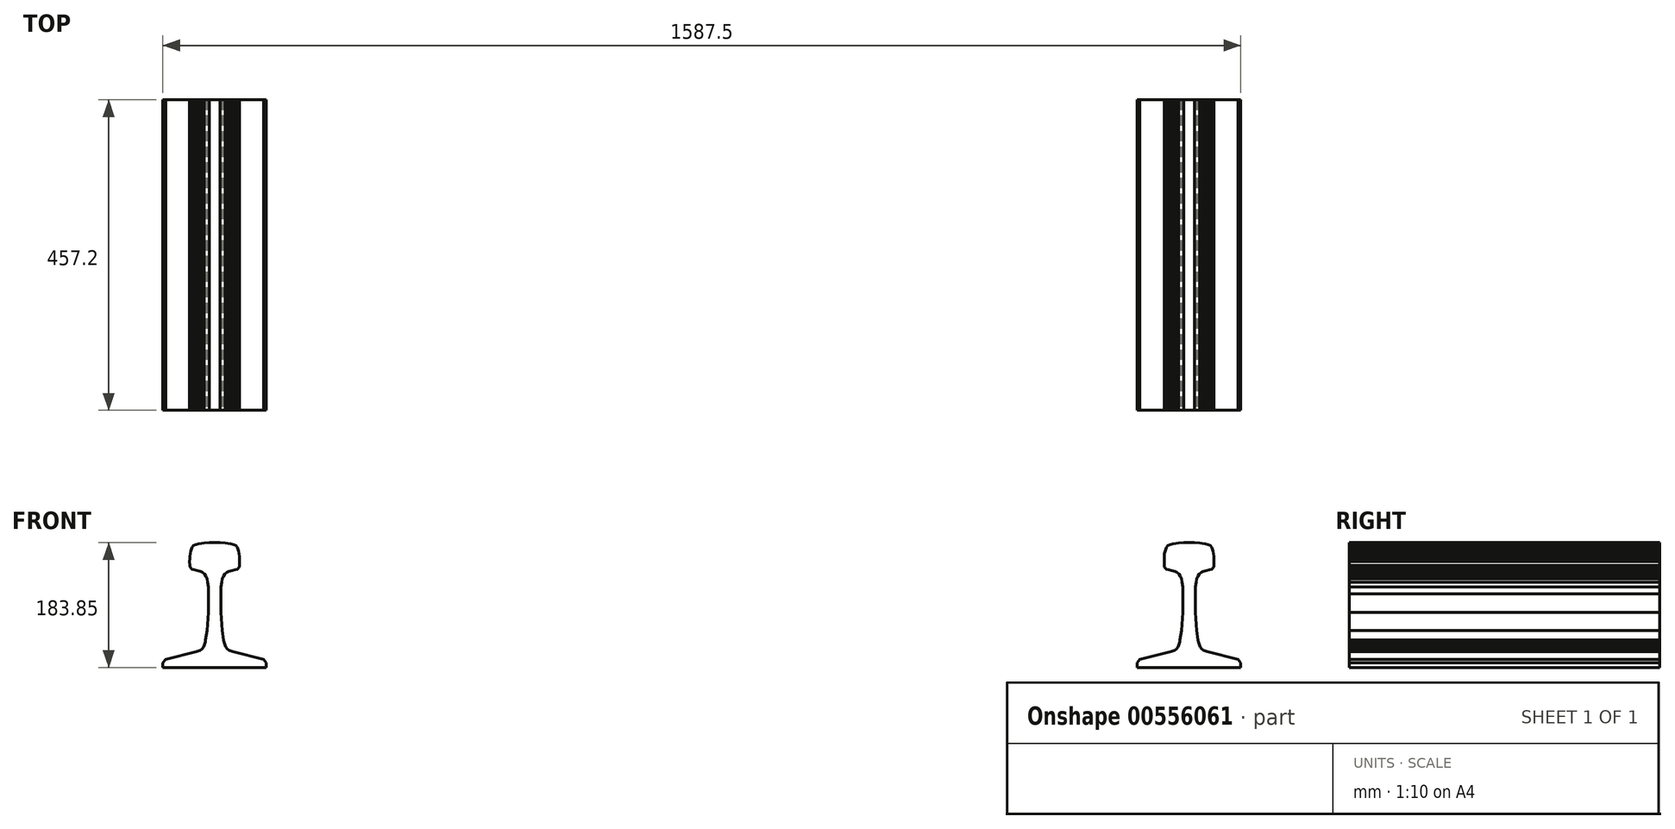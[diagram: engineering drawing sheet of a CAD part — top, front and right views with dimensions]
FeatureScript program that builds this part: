
annotation { "Feature Type Name" : "Feature", "Feature Type Description" : "" }
export const myFeature = defineFeature(function(context is Context, id is Id, definition is map)
    precondition{}
    {
        {
            var Q0;
            Q0=qCreatedBy(makeId("Front.planeOp"),FACE);
            var sketch = newSketch(context, id + "F0", { "sketchPlane" : qUnion([Q0])});
            skLineSegment(sketch, "E0", {"start": v(-76.2, -57.1) * mm, "end": v(76.2, -57.1) * mm});
            skLineSegment(sketch, "E1", {"start": v(-76.2, -57.1) * mm, "end": v(-76.2, -46.22) * mm});
            skLineSegment(sketch, "E2", {"start": v(-26.84, -33.73) * mm, "end": v(-76.2, -46.22) * mm});
            skPoint(sketch, "E3.startSnap0", {"position": v(0, -57.1) * mm});
            skPoint(sketch, "E3.endSnap0", {"position": v(0, -57.1) * mm});
            skLineSegment(sketch, "E4.MirrorCS", {"start": v(26.84, -33.73) * mm, "end": v(76.2, -46.22) * mm});
            skLineSegment(sketch, "E5.MirrorCS", {"start": v(0, -26.94) * mm, "end": v(0, -26.94) * mm});
            skLineSegment(sketch, "E6.MirrorCS", {"start": v(76.2, -57.1) * mm, "end": v(76.2, -46.22) * mm});
            skLineSegment(sketch, "E7", {"start": v(-26.84, -33.73) * mm, "end": v(-21.16, -31.84) * mm});
            skLineSegment(sketch, "E8", {"start": v(-21.16, -31.84) * mm, "end": v(-18.7, -29.61) * mm});
            skLineSegment(sketch, "E9", {"start": v(-18.7, -29.61) * mm, "end": v(-16.22, -26.55) * mm});
            skLineSegment(sketch, "E10", {"start": v(-16.22, -26.55) * mm, "end": v(-14.69, -22.9) * mm});
            skLineSegment(sketch, "E11", {"start": v(-14.69, -22.9) * mm, "end": v(-13.49, -19.14) * mm});
            skLineSegment(sketch, "E12", {"start": v(-13.49, -19.14) * mm, "end": v(-13.3, -16.85) * mm});
            skLineSegment(sketch, "E13", {"start": v(-13.3, -16.85) * mm, "end": v(-10.94, -2.66) * mm});
            skLineSegment(sketch, "E14", {"start": v(-10.94, -2.66) * mm, "end": v(-9.17, 23.94) * mm});
            skLineSegment(sketch, "E15", {"start": v(-9.17, 23.94) * mm, "end": v(-9.1, 51.27) * mm});
            skLineSegment(sketch, "E16", {"start": v(-9.1, 51.27) * mm, "end": v(-9.47, 61.37) * mm});
            skLineSegment(sketch, "E17", {"start": v(-36.63, 93.52) * mm, "end": v(-36.6, 93.52) * mm});
            skLineSegment(sketch, "E18", {"start": v(-9.47, 61.37) * mm, "end": v(-10.2, 68.53) * mm});
            skLineSegment(sketch, "E19", {"start": v(-10.2, 68.53) * mm, "end": v(-11.42, 73.4) * mm});
            skLineSegment(sketch, "E20", {"start": v(-11.42, 73.4) * mm, "end": v(-12.99, 77.66) * mm});
            skLineSegment(sketch, "E21", {"start": v(-12.99, 77.66) * mm, "end": v(-14.98, 80.45) * mm});
            skLineSegment(sketch, "E22", {"start": v(-14.98, 80.45) * mm, "end": v(-18.1, 83) * mm});
            skLineSegment(sketch, "E23", {"start": v(-18.1, 83) * mm, "end": v(-20.68, 84.15) * mm});
            skLineSegment(sketch, "E24", {"start": v(-20.68, 84.15) * mm, "end": v(-25.92, 85.98) * mm});
            skLineSegment(sketch, "E25", {"start": v(-25.92, 85.98) * mm, "end": v(-30.18, 87.13) * mm});
            skLineSegment(sketch, "E26", {"start": v(-30.18, 87.13) * mm, "end": v(-33.1, 87.75) * mm});
            skLineSegment(sketch, "E27", {"start": v(-33.1, 87.75) * mm, "end": v(-34.18, 88.3) * mm});
            skLineSegment(sketch, "E28", {"start": v(-34.18, 88.3) * mm, "end": v(-35.39, 89.62) * mm});
            skLineSegment(sketch, "E29", {"start": v(-35.39, 89.62) * mm, "end": v(-36.17, 91) * mm});
            skLineSegment(sketch, "E30", {"start": v(-36.17, 91) * mm, "end": v(-36.4, 91.97) * mm});
            skLineSegment(sketch, "E31", {"start": v(-36.4, 91.97) * mm, "end": v(-36.6, 93.51) * mm});
            skLineSegment(sketch, "E32", {"start": v(-36.6, 93.51) * mm, "end": v(-36.83, 98.88) * mm});
            skLineSegment(sketch, "E33", {"start": v(-36.83, 98.88) * mm, "end": v(-36.67, 103.67) * mm});
            skLineSegment(sketch, "E34", {"start": v(-36.67, 103.67) * mm, "end": v(-36.4, 106.65) * mm});
            skLineSegment(sketch, "E35", {"start": v(-36.4, 106.65) * mm, "end": v(-36.18, 110.32) * mm});
            skLineSegment(sketch, "E36", {"start": v(-36.18, 110.32) * mm, "end": v(-35.56, 114.28) * mm});
            skLineSegment(sketch, "E37", {"start": v(-35.56, 114.28) * mm, "end": v(-34.24, 117.98) * mm});
            skLineSegment(sketch, "E38", {"start": v(-34.24, 117.98) * mm, "end": v(-33.33, 119.88) * mm});
            skLineSegment(sketch, "E39", {"start": v(-33.33, 119.88) * mm, "end": v(-31.13, 122.46) * mm});
            skLineSegment(sketch, "E40", {"start": v(-31.13, 122.46) * mm, "end": v(-28.22, 124.04) * mm});
            skLineSegment(sketch, "E41", {"start": v(-28.22, 124.04) * mm, "end": v(-24.03, 125.35) * mm});
            skLineSegment(sketch, "E42", {"start": v(-24.03, 125.35) * mm, "end": v(-19.54, 126) * mm});
            skLineSegment(sketch, "E43.MirrorCS", {"start": v(36.4, 91.97) * mm, "end": v(36.6, 93.51) * mm});
            skLineSegment(sketch, "E44.MirrorCS", {"start": v(36.17, 91) * mm, "end": v(36.4, 91.97) * mm});
            skLineSegment(sketch, "E45.MirrorCS", {"start": v(13.49, -19.14) * mm, "end": v(13.3, -16.85) * mm});
            skLineSegment(sketch, "E46.MirrorCS", {"start": v(36.67, 103.67) * mm, "end": v(36.4, 106.65) * mm});
            skLineSegment(sketch, "E47.MirrorCS", {"start": v(20.68, 84.15) * mm, "end": v(25.92, 85.98) * mm});
            skLineSegment(sketch, "E48.MirrorCS", {"start": v(31.13, 122.46) * mm, "end": v(28.22, 124.04) * mm});
            skLineSegment(sketch, "E49.MirrorCS", {"start": v(36.6, 93.51) * mm, "end": v(36.83, 98.88) * mm});
            skLineSegment(sketch, "E50.MirrorCS", {"start": v(16.22, -26.55) * mm, "end": v(14.69, -22.9) * mm});
            skLineSegment(sketch, "E51.MirrorCS", {"start": v(34.18, 88.3) * mm, "end": v(35.39, 89.62) * mm});
            skLineSegment(sketch, "E52.MirrorCS", {"start": v(14.69, -22.9) * mm, "end": v(13.49, -19.14) * mm});
            skLineSegment(sketch, "E53.MirrorCS", {"start": v(12.99, 77.66) * mm, "end": v(14.98, 80.45) * mm});
            skLineSegment(sketch, "E54.MirrorCS", {"start": v(35.56, 114.28) * mm, "end": v(34.24, 117.98) * mm});
            skLineSegment(sketch, "E55.MirrorCS", {"start": v(28.22, 124.04) * mm, "end": v(24.03, 125.35) * mm});
            skLineSegment(sketch, "E56.MirrorCS", {"start": v(25.92, 85.98) * mm, "end": v(30.18, 87.13) * mm});
            skLineSegment(sketch, "E57.MirrorCS", {"start": v(26.84, -33.73) * mm, "end": v(21.16, -31.84) * mm});
            skLineSegment(sketch, "E58.MirrorCS", {"start": v(18.1, 83) * mm, "end": v(20.68, 84.15) * mm});
            skLineSegment(sketch, "E59.MirrorCS", {"start": v(21.16, -31.84) * mm, "end": v(18.7, -29.61) * mm});
            skLineSegment(sketch, "E60.MirrorCS", {"start": v(14.98, 80.45) * mm, "end": v(18.1, 83) * mm});
            skLineSegment(sketch, "E61.MirrorCS", {"start": v(33.1, 87.75) * mm, "end": v(34.18, 88.3) * mm});
            skLineSegment(sketch, "E62.MirrorCS", {"start": v(33.33, 119.88) * mm, "end": v(31.13, 122.46) * mm});
            skLineSegment(sketch, "E63.MirrorCS", {"start": v(30.18, 87.13) * mm, "end": v(33.1, 87.75) * mm});
            skLineSegment(sketch, "E64.MirrorCS", {"start": v(10.2, 68.53) * mm, "end": v(11.42, 73.4) * mm});
            skLineSegment(sketch, "E65.MirrorCS", {"start": v(34.24, 117.98) * mm, "end": v(33.33, 119.88) * mm});
            skLineSegment(sketch, "E66.MirrorCS", {"start": v(11.42, 73.4) * mm, "end": v(12.99, 77.66) * mm});
            skLineSegment(sketch, "E67.MirrorCS", {"start": v(24.03, 125.35) * mm, "end": v(19.54, 126) * mm});
            skLineSegment(sketch, "E68.MirrorCS", {"start": v(18.7, -29.61) * mm, "end": v(16.22, -26.55) * mm});
            skLineSegment(sketch, "E69.MirrorCS", {"start": v(35.39, 89.62) * mm, "end": v(36.17, 91) * mm});
            skLineSegment(sketch, "E70.MirrorCS", {"start": v(36.18, 110.32) * mm, "end": v(35.56, 114.28) * mm});
            skLineSegment(sketch, "E71.MirrorCS", {"start": v(36.4, 106.65) * mm, "end": v(36.18, 110.32) * mm});
            skLineSegment(sketch, "E72.MirrorCS", {"start": v(9.47, 61.37) * mm, "end": v(10.2, 68.53) * mm});
            skLineSegment(sketch, "E73.MirrorCS", {"start": v(15.45, 126.6) * mm, "end": v(15.43, 126.61) * mm});
            skLineSegment(sketch, "E74.MirrorCS", {"start": v(36.83, 98.88) * mm, "end": v(36.67, 103.67) * mm});
            skLineSegment(sketch, "E75.MirrorCS", {"start": v(10.94, -2.66) * mm, "end": v(9.17, 23.94) * mm});
            skLineSegment(sketch, "E76.MirrorCS", {"start": v(9.1, 51.27) * mm, "end": v(9.47, 61.37) * mm});
            skLineSegment(sketch, "E77.MirrorCS", {"start": v(13.3, -16.85) * mm, "end": v(10.94, -2.66) * mm});
            skLineSegment(sketch, "E78.MirrorCS", {"start": v(9.17, 23.94) * mm, "end": v(9.1, 51.27) * mm});
            skPoint(sketch, "E79.start.orphan", {"position": v(-15.43, 126.61) * mm});
            skLineSegment(sketch, "E80", {"start": v(-19.54, 126) * mm, "end": v(-15.43, 126.4) * mm});
            skLineSegment(sketch, "E81", {"start": v(-15.43, 126.4) * mm, "end": v(-8, 126.76) * mm});
            skLineSegment(sketch, "E82", {"start": v(-8, 126.76) * mm, "end": v(0, 126.76) * mm});
            skLineSegment(sketch, "E83.MirrorCS", {"start": v(8, 126.76) * mm, "end": v(0, 126.76) * mm});
            skLineSegment(sketch, "E84.MirrorCS", {"start": v(15.43, 126.4) * mm, "end": v(8, 126.76) * mm});
            skLineSegment(sketch, "E85.MirrorCS", {"start": v(19.54, 126) * mm, "end": v(15.43, 126.4) * mm});
            skPoint(sketch, "E86.orphan", {"position": v(-76.2, -26.94) * mm});
            skPoint(sketch, "E87.orphan", {"position": v(-31.72, -14.5) * mm});
            skPoint(sketch, "E88.end.orphan", {"position": v(-76.21, 41.14) * mm});
            skPoint(sketch, "E88.start.orphan", {"position": v(-76.21, -8.79) * mm});
            skLineSegment(sketch, "E89", {"start": v(76.2, -57.1) * mm, "end": v(76.2, -57.1) * mm});
            skPoint(sketch, "E90.orphan", {"position": v(76.2, -26.94) * mm});
            skPoint(sketch, "E91.MirrorCS.end.orphan", {"position": v(76.21, -8.79) * mm});
            skPoint(sketch, "E91.MirrorCS.start.orphan", {"position": v(31.72, -14.5) * mm});
            skPoint(sketch, "E92.orphan", {"position": v(0, -26.94) * mm});
            skLineSegment(sketch, "E93.trimOffspring", {"start": v(36.6, 93.52) * mm, "end": v(37.03, 93.52) * mm});
            skPoint(sketch, "E94.trimOffspring.end.orphan", {"position": v(0, 152.1) * mm});
            skPoint(sketch, "E3.start.orphan", {"position": v(0, -57.1) * mm});
            skLineSegment(sketch, "E95.MirrorCS", {"start": v(1470.49, 89.62) * mm, "end": v(1471.27, 91) * mm});
            skLineSegment(sketch, "E96.MirrorCS", {"start": v(1471.73, 93.52) * mm, "end": v(1471.7, 93.52) * mm});
            skLineSegment(sketch, "E97.MirrorCS", {"start": v(1468.2, 87.75) * mm, "end": v(1469.28, 88.3) * mm});
            skLineSegment(sketch, "E98.MirrorCS", {"start": v(1471.27, 91) * mm, "end": v(1471.5, 91.97) * mm});
            skLineSegment(sketch, "E99.MirrorCS", {"start": v(1469.28, 88.3) * mm, "end": v(1470.49, 89.62) * mm});
            skLineSegment(sketch, "E100.MirrorCS", {"start": v(1471.5, 91.97) * mm, "end": v(1471.7, 93.51) * mm});
            skLineSegment(sketch, "E101.MirrorCS", {"start": v(1471.93, 98.88) * mm, "end": v(1471.77, 103.67) * mm});
            skLineSegment(sketch, "E102.MirrorCS", {"start": v(1461.02, 85.98) * mm, "end": v(1465.28, 87.13) * mm});
            skLineSegment(sketch, "E103.MirrorCS", {"start": v(1465.28, 87.13) * mm, "end": v(1468.2, 87.75) * mm});
            skLineSegment(sketch, "E104.MirrorCS", {"start": v(1471.7, 93.51) * mm, "end": v(1471.93, 98.88) * mm});
            skLineSegment(sketch, "E105.MirrorCS", {"start": v(1471.77, 103.67) * mm, "end": v(1471.5, 106.65) * mm});
            skLineSegment(sketch, "E106.MirrorCS", {"start": v(1470.66, 114.28) * mm, "end": v(1469.34, 117.98) * mm});
            skLineSegment(sketch, "E107.MirrorCS", {"start": v(1398.93, 91) * mm, "end": v(1398.7, 91.97) * mm});
            skLineSegment(sketch, "E108.MirrorCS", {"start": v(1398.7, 91.97) * mm, "end": v(1398.5, 93.51) * mm});
            skLineSegment(sketch, "E109.MirrorCS", {"start": v(1469.34, 117.98) * mm, "end": v(1468.43, 119.88) * mm});
            skLineSegment(sketch, "E110.MirrorCS", {"start": v(1471.5, 106.65) * mm, "end": v(1471.28, 110.32) * mm});
            skLineSegment(sketch, "E111.MirrorCS", {"start": v(1400.92, 88.3) * mm, "end": v(1399.71, 89.62) * mm});
            skLineSegment(sketch, "E112.MirrorCS", {"start": v(1471.28, 110.32) * mm, "end": v(1470.66, 114.28) * mm});
            skLineSegment(sketch, "E113.MirrorCS", {"start": v(1404.92, 87.13) * mm, "end": v(1402, 87.75) * mm});
            skLineSegment(sketch, "E114.MirrorCS", {"start": v(1466.23, 122.46) * mm, "end": v(1463.32, 124.04) * mm});
            skLineSegment(sketch, "E115.MirrorCS", {"start": v(1402, 87.75) * mm, "end": v(1400.92, 88.3) * mm});
            skLineSegment(sketch, "E116.MirrorCS", {"start": v(1398.5, 93.51) * mm, "end": v(1398.27, 98.88) * mm});
            skLineSegment(sketch, "E117.MirrorCS", {"start": v(1409.18, 85.98) * mm, "end": v(1404.92, 87.13) * mm});
            skLineSegment(sketch, "E118.MirrorCS", {"start": v(1358.9, -57.1) * mm, "end": v(1358.9, -46.22) * mm});
            skLineSegment(sketch, "E119.MirrorCS", {"start": v(1398.5, 93.52) * mm, "end": v(1398.07, 93.52) * mm});
            skLineSegment(sketch, "E120.MirrorCS", {"start": v(1398.27, 98.88) * mm, "end": v(1398.43, 103.67) * mm});
            skLineSegment(sketch, "E121.MirrorCS", {"start": v(1399.71, 89.62) * mm, "end": v(1398.93, 91) * mm});
            skLineSegment(sketch, "E122.MirrorCS", {"start": v(1468.43, 119.88) * mm, "end": v(1466.23, 122.46) * mm});
            skLineSegment(sketch, "E123.MirrorCS", {"start": v(1450.08, 80.45) * mm, "end": v(1453.2, 83) * mm});
            skLineSegment(sketch, "E124.MirrorCS", {"start": v(1419.65, 126.6) * mm, "end": v(1419.67, 126.61) * mm});
            skLineSegment(sketch, "E125.MirrorCS", {"start": v(1451.32, -26.55) * mm, "end": v(1449.79, -22.9) * mm});
            skLineSegment(sketch, "E126.MirrorCS", {"start": v(1420.41, -22.9) * mm, "end": v(1421.61, -19.14) * mm});
            skLineSegment(sketch, "E127.MirrorCS", {"start": v(1400.86, 117.98) * mm, "end": v(1401.77, 119.88) * mm});
            skLineSegment(sketch, "E128.MirrorCS", {"start": v(1418.88, -26.55) * mm, "end": v(1420.41, -22.9) * mm});
            skLineSegment(sketch, "E129.MirrorCS", {"start": v(1456.26, -31.84) * mm, "end": v(1453.8, -29.61) * mm});
            skLineSegment(sketch, "E130.MirrorCS", {"start": v(1449.79, -22.9) * mm, "end": v(1448.59, -19.14) * mm});
            skLineSegment(sketch, "E131.MirrorCS", {"start": v(1448.59, -19.14) * mm, "end": v(1448.4, -16.85) * mm});
            skLineSegment(sketch, "E132.MirrorCS", {"start": v(1421.61, -19.14) * mm, "end": v(1421.8, -16.85) * mm});
            skLineSegment(sketch, "E133.MirrorCS", {"start": v(1403.97, 122.46) * mm, "end": v(1406.88, 124.04) * mm});
            skLineSegment(sketch, "E134.MirrorCS", {"start": v(1448.09, 77.66) * mm, "end": v(1450.08, 80.45) * mm});
            skLineSegment(sketch, "E135.MirrorCS", {"start": v(1463.32, 124.04) * mm, "end": v(1459.13, 125.35) * mm});
            skLineSegment(sketch, "E136.MirrorCS", {"start": v(1423.68, 73.4) * mm, "end": v(1422.11, 77.66) * mm});
            skLineSegment(sketch, "E137.MirrorCS", {"start": v(1398.7, 106.65) * mm, "end": v(1398.92, 110.32) * mm});
            skLineSegment(sketch, "E138.MirrorCS", {"start": v(1399.54, 114.28) * mm, "end": v(1400.86, 117.98) * mm});
            skLineSegment(sketch, "E139.MirrorCS", {"start": v(1419.67, 126.4) * mm, "end": v(1427.1, 126.76) * mm});
            skLineSegment(sketch, "E140.MirrorCS", {"start": v(1461.94, -33.73) * mm, "end": v(1456.26, -31.84) * mm});
            skLineSegment(sketch, "E141.MirrorCS", {"start": v(1406.88, 124.04) * mm, "end": v(1411.07, 125.35) * mm});
            skLineSegment(sketch, "E142.MirrorCS", {"start": v(1413.94, -31.84) * mm, "end": v(1416.4, -29.61) * mm});
            skLineSegment(sketch, "E143.MirrorCS", {"start": v(1398.43, 103.67) * mm, "end": v(1398.7, 106.65) * mm});
            skLineSegment(sketch, "E144.MirrorCS", {"start": v(1411.07, 125.35) * mm, "end": v(1415.56, 126) * mm});
            skLineSegment(sketch, "E145.MirrorCS", {"start": v(1453.2, 83) * mm, "end": v(1455.78, 84.15) * mm});
            skLineSegment(sketch, "E146.MirrorCS", {"start": v(1446.52, 73.4) * mm, "end": v(1448.09, 77.66) * mm});
            skLineSegment(sketch, "E147.MirrorCS", {"start": v(1455.78, 84.15) * mm, "end": v(1461.02, 85.98) * mm});
            skLineSegment(sketch, "E148.MirrorCS", {"start": v(1417, 83) * mm, "end": v(1414.42, 84.15) * mm});
            skLineSegment(sketch, "E149.MirrorCS", {"start": v(1398.92, 110.32) * mm, "end": v(1399.54, 114.28) * mm});
            skLineSegment(sketch, "E150.MirrorCS", {"start": v(1453.8, -29.61) * mm, "end": v(1451.32, -26.55) * mm});
            skLineSegment(sketch, "E151.MirrorCS", {"start": v(1415.56, 126) * mm, "end": v(1419.67, 126.4) * mm});
            skLineSegment(sketch, "E152.MirrorCS", {"start": v(1454.64, 126) * mm, "end": v(1450.53, 126.4) * mm});
            skLineSegment(sketch, "E153.MirrorCS", {"start": v(1416.4, -29.61) * mm, "end": v(1418.88, -26.55) * mm});
            skLineSegment(sketch, "E154.MirrorCS", {"start": v(1401.77, 119.88) * mm, "end": v(1403.97, 122.46) * mm});
            skLineSegment(sketch, "E155.MirrorCS", {"start": v(1448.4, -16.85) * mm, "end": v(1446.04, -2.66) * mm});
            skLineSegment(sketch, "E156.MirrorCS", {"start": v(1425.63, 61.37) * mm, "end": v(1424.9, 68.53) * mm});
            skLineSegment(sketch, "E157.MirrorCS", {"start": v(1427.1, 126.76) * mm, "end": v(1435.1, 126.76) * mm});
            skLineSegment(sketch, "E158.MirrorCS", {"start": v(1424.9, 68.53) * mm, "end": v(1423.68, 73.4) * mm});
            skLineSegment(sketch, "E159.MirrorCS", {"start": v(1443.1, 126.76) * mm, "end": v(1435.1, 126.76) * mm});
            skLineSegment(sketch, "E160.MirrorCS", {"start": v(1444.57, 61.37) * mm, "end": v(1445.3, 68.53) * mm});
            skLineSegment(sketch, "E161.MirrorCS", {"start": v(1450.53, 126.4) * mm, "end": v(1443.1, 126.76) * mm});
            skLineSegment(sketch, "E162.MirrorCS", {"start": v(1420.12, 80.45) * mm, "end": v(1417, 83) * mm});
            skLineSegment(sketch, "E163.MirrorCS", {"start": v(1408.26, -33.73) * mm, "end": v(1413.94, -31.84) * mm});
            skLineSegment(sketch, "E164.MirrorCS", {"start": v(1459.13, 125.35) * mm, "end": v(1454.64, 126) * mm});
            skLineSegment(sketch, "E165.MirrorCS", {"start": v(1445.3, 68.53) * mm, "end": v(1446.52, 73.4) * mm});
            skLineSegment(sketch, "E166.MirrorCS", {"start": v(1422.11, 77.66) * mm, "end": v(1420.12, 80.45) * mm});
            skLineSegment(sketch, "E167.MirrorCS", {"start": v(1444.2, 51.27) * mm, "end": v(1444.57, 61.37) * mm});
            skLineSegment(sketch, "E168.MirrorCS", {"start": v(1421.8, -16.85) * mm, "end": v(1424.16, -2.66) * mm});
            skLineSegment(sketch, "E169.MirrorCS", {"start": v(1414.42, 84.15) * mm, "end": v(1409.18, 85.98) * mm});
            skLineSegment(sketch, "E170.MirrorCS", {"start": v(1446.04, -2.66) * mm, "end": v(1444.27, 23.94) * mm});
            skPoint(sketch, "E171.MirrorP", {"position": v(1435.1, -57.1) * mm});
            skLineSegment(sketch, "E172.MirrorCS", {"start": v(1424.16, -2.66) * mm, "end": v(1425.93, 23.94) * mm});
            skLineSegment(sketch, "E173.MirrorCS", {"start": v(1426, 51.27) * mm, "end": v(1425.63, 61.37) * mm});
            skLineSegment(sketch, "E174.MirrorCS", {"start": v(1511.3, -57.1) * mm, "end": v(1511.3, -46.22) * mm});
            skLineSegment(sketch, "E175.MirrorCS", {"start": v(1358.9, -57.1) * mm, "end": v(1358.9, -57.1) * mm});
            skPoint(sketch, "E176.MirrorP", {"position": v(1435.1, -26.94) * mm});
            skPoint(sketch, "E177.MirrorP", {"position": v(1358.9, -26.94) * mm});
            skPoint(sketch, "E178.MirrorP", {"position": v(1511.3, -26.94) * mm});
            skPoint(sketch, "E179.MirrorP", {"position": v(1466.82, -14.5) * mm});
            skLineSegment(sketch, "E180.MirrorCS", {"start": v(1425.93, 23.94) * mm, "end": v(1426, 51.27) * mm});
            skPoint(sketch, "E181.MirrorP", {"position": v(1450.53, 126.61) * mm});
            skPoint(sketch, "E182.MirrorP", {"position": v(1358.89, -8.79) * mm});
            skLineSegment(sketch, "E183.MirrorCS", {"start": v(1444.27, 23.94) * mm, "end": v(1444.2, 51.27) * mm});
            skPoint(sketch, "E184.MirrorP", {"position": v(1403.38, -14.5) * mm});
            skLineSegment(sketch, "E185.MirrorCS", {"start": v(1461.94, -33.73) * mm, "end": v(1511.3, -46.22) * mm});
            skPoint(sketch, "E186.MirrorP", {"position": v(1511.31, -8.79) * mm});
            skLineSegment(sketch, "E187.MirrorCS", {"start": v(1435.1, -26.94) * mm, "end": v(1435.1, -26.94) * mm});
            skPoint(sketch, "E188.MirrorP", {"position": v(1511.31, 41.14) * mm});
            skLineSegment(sketch, "E189.MirrorCS", {"start": v(1511.3, -57.1) * mm, "end": v(1358.9, -57.1) * mm});
            skLineSegment(sketch, "E190.MirrorCS", {"start": v(1408.26, -33.73) * mm, "end": v(1358.9, -46.22) * mm});
            skPoint(sketch, "E191.MirrorP", {"position": v(1435.1, 152.1) * mm});
            skSolve(sketch);
        }
        {
            var Q0;
            Q0=qSketchRegion(id+"F0",true);
            extrude(context, id + "F1", {"entities" : qUnion([Q0]), "oppositeDirection" : true, "depth" : 457.2 * mm, "offsetDistance" : 25.4 * mm});
        }
        {
            var Q0;
            Q0=makeQuery(id+"F1.opExtrude","SWEPT_EDGE",EDGE,{"disambiguationData":[OSD([sQuery(id+"F0.wireOp",EDGE,"E4.MirrorCS"),sQuery(id+"F0.wireOp",EDGE,"E6.MirrorCS")])]});
            var Q1;
            Q1=makeQuery(id+"F1.opExtrude","SWEPT_EDGE",EDGE,{"disambiguationData":[OSD([sQuery(id+"F0.wireOp",EDGE,"E1"),sQuery(id+"F0.wireOp",EDGE,"E2")])]});
            var Q2;
            Q2=makeQuery(id+"F1.opExtrude","SWEPT_EDGE",EDGE,{"disambiguationData":[OSD([sQuery(id+"F0.wireOp",EDGE,"E118.MirrorCS"),sQuery(id+"F0.wireOp",EDGE,"E190.MirrorCS")])]});
            var Q3;
            Q3=makeQuery(id+"F1.opExtrude","SWEPT_EDGE",EDGE,{"disambiguationData":[OSD([sQuery(id+"F0.wireOp",EDGE,"E174.MirrorCS"),sQuery(id+"F0.wireOp",EDGE,"E185.MirrorCS")])]});
            chamfer(context, id + "F2", {"entities" : qUnion([Q0, Q1, Q2, Q3]), "width" : 5.08 * mm, "tangentPropagation" : true});
        }
    });
